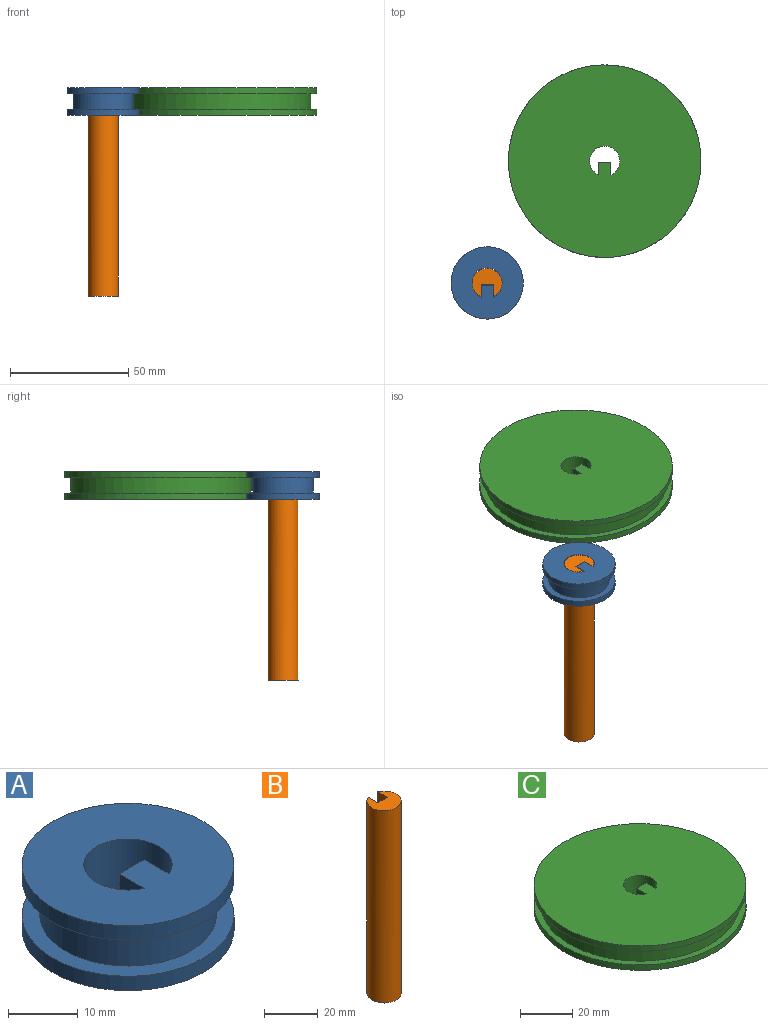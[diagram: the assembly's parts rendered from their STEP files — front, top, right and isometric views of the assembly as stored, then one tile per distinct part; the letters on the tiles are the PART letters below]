
ASSEMBLY  parts=3 mates=2
PART A: 11 faces, bbox 30.5x30.5x11.4 mm
  f0: cylinder r=15.24mm len=30.48mm, axis (0,0,-1), area 243.2mm2, adj f1,f2
  f1: plane 30.48x30.48mm, normal (0,0,1), area 630.6mm2, adj f0,f7,f8,f9,f10
  f2: plane 30.48x30.48mm, normal (0,0,-1), area 223mm2, adj f0,f6
  f3: cylinder r=15.24mm len=30.48mm, axis (0,0,1), area 243.2mm2, adj f4,f5
  f4: plane 30.48x30.48mm, normal (0,0,-1), area 630.6mm2, adj f3,f7,f8,f9,f10
  f5: plane 30.48x30.48mm, normal (0,0,1), area 223mm2, adj f3,f6
  f6: cylinder r=12.7mm len=25.4mm, axis (0,0,-1), area 506.7mm2, adj f2,f5
  f7: cylinder r=6.35mm len=12.7mm, axis (0,0,1), area 396.3mm2, adj f1,f4,f8,f10
  f8: plane 11.43x5.08mm, normal (-1,0,0), area 58.1mm2, adj f1,f4,f7,f9
  f9: plane 11.43x5.08mm, normal (0,1,0), area 58.1mm2, adj f1,f4,f8,f10
  f10: plane 11.43x5.08mm, normal (1,0,0), area 58.1mm2, adj f1,f4,f7,f9
PART B: 7 faces, bbox 12.7x12.7x87.6 mm
  f0: plane 11.43x5.08mm, normal (0,1,0), area 58.1mm2, adj f1,f3,f4,f5
  f1: plane 11.43x5.08mm, normal (1,0,0), area 58.1mm2, adj f0,f2,f4,f5
  f2: cylinder r=6.35mm len=87.63mm, axis (0,0,-1), area 3436.5mm2, adj f1,f3,f4,f5,f6
  f3: plane 11.43x5.08mm, normal (-1,0,0), area 58.1mm2, adj f0,f2,f4,f5
  f4: plane 12.7x12.17mm, normal (0,0,1), area 99.1mm2, adj f0,f1,f2,f3
  f5: plane 5.61x5.08mm, normal (0,0,1), area 27.6mm2, adj f0,f1,f2,f3
  f6: plane 12.7x12.7mm, normal (0,0,-1), area 126.7mm2, adj f2
PART C: 11 faces, bbox 81.3x81.3x11.4 mm
  f0: cylinder r=40.64mm len=81.28mm, axis (0,0,-1), area 648.6mm2, adj f1,f2
  f1: plane 81.28x81.28mm, normal (0,0,1), area 5089.6mm2, adj f0,f7,f8,f9,f10
  f2: plane 81.28x81.28mm, normal (0,0,-1), area 628.3mm2, adj f0,f6
  f3: cylinder r=40.64mm len=81.28mm, axis (0,0,1), area 648.6mm2, adj f4,f5
  f4: plane 81.28x81.28mm, normal (0,0,-1), area 5089.6mm2, adj f3,f7,f8,f9,f10
  f5: plane 81.28x81.28mm, normal (0,0,1), area 628.3mm2, adj f3,f6
  f6: cylinder r=38.1mm len=76.2mm, axis (0,0,-1), area 1520.1mm2, adj f2,f5
  f7: cylinder r=6.35mm len=12.7mm, axis (0,0,1), area 396.3mm2, adj f1,f4,f8,f10
  f8: plane 11.43x5.08mm, normal (-1,0,0), area 58.1mm2, adj f1,f4,f7,f9
  f9: plane 11.43x5.08mm, normal (0,1,0), area 58.1mm2, adj f1,f4,f8,f10
  f10: plane 11.43x5.08mm, normal (1,0,0), area 58.1mm2, adj f1,f4,f7,f9
PLACE A t=(15.34,-40.25,-1.92)mm
PLACE B rot(axis=(0,0,1),180deg) t=(-29.29,-40.4,-4.67)mm fixed
PLACE C t=(-10.63,11.16,-1.92)mm
MATE slider A.f1 <-> B.f2  axis (0,0,1) through (-29.29,-40.4,6.97)mm
MATE planar A.f1 <-> C.f1  axis (0,0,1) through (-26.75,-40.99,6.97)mm
